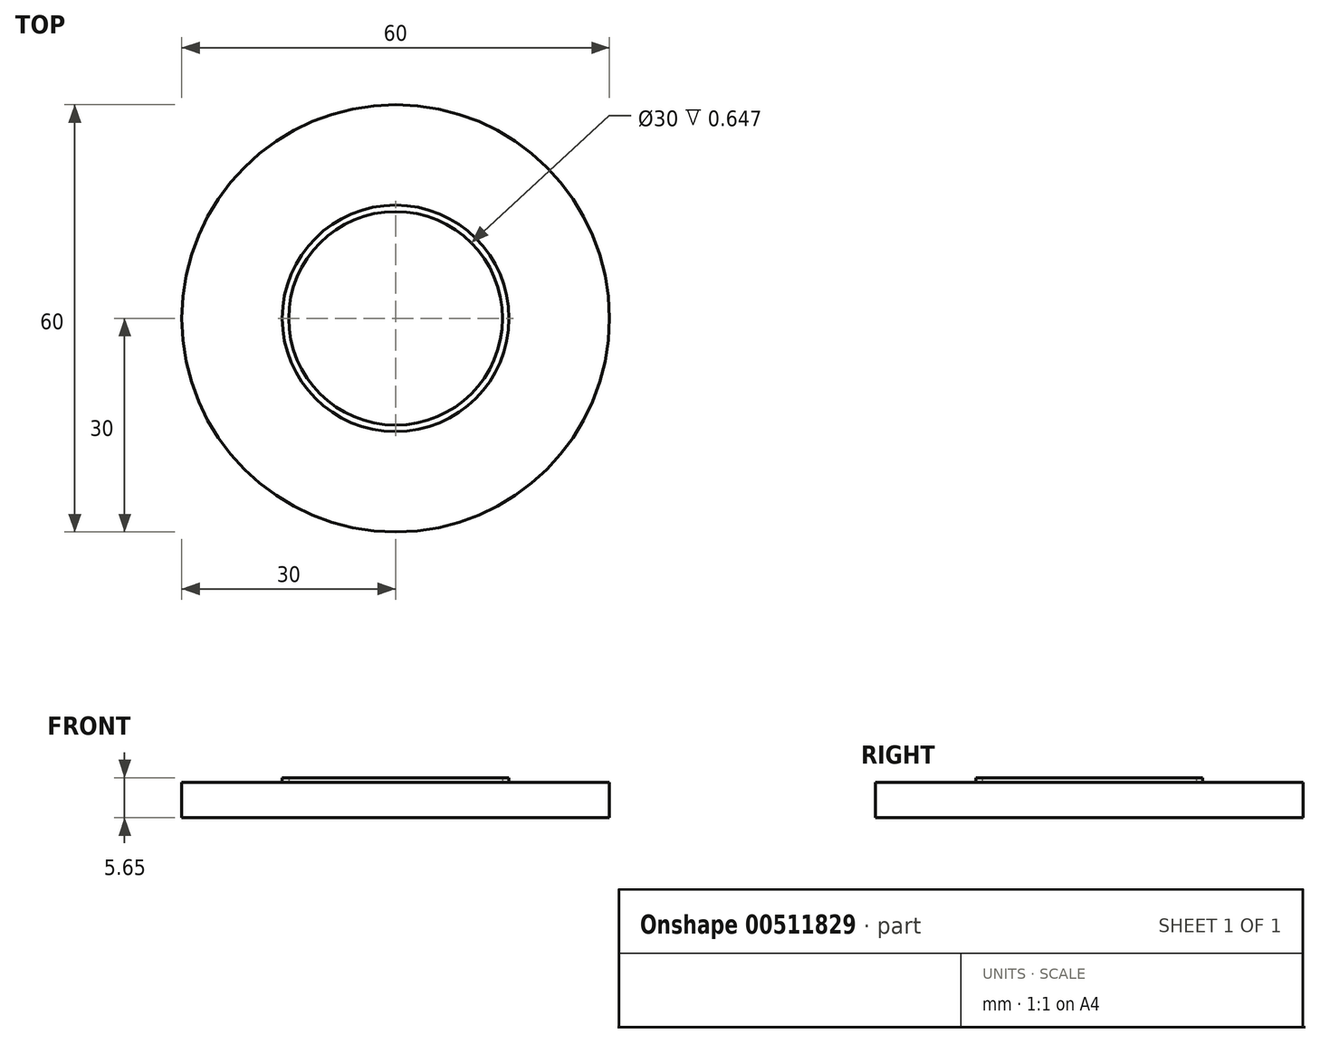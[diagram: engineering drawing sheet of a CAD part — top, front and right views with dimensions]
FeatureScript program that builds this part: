
annotation { "Feature Type Name" : "Feature", "Feature Type Description" : "" }
export const myFeature = defineFeature(function(context is Context, id is Id, definition is map)
    precondition{}
    {
        {
            var Q0;
            Q0=qCreatedBy(makeId("Front.planeOp"),FACE);
            var sketch = newSketch(context, id + "F0", { "sketchPlane" : qUnion([Q0])});
            skLineSegment(sketch, "E0", {"start": v(0, 0) * mm, "end": v(0, 26.23) * mm, "construction": true});
            skPoint(sketch, "E1.end.orphan", {"position": v(106.03, -6.74) * mm});
            skPoint(sketch, "E2.end.orphan", {"position": v(0, -6.74) * mm});
            skLineSegment(sketch, "E3.bottom", {"start": v(0, 0) * mm, "end": v(30, 0) * mm});
            skLineSegment(sketch, "E3.top", {"start": v(0, -5) * mm, "end": v(30, -5) * mm});
            skLineSegment(sketch, "E3.left", {"start": v(0, 0) * mm, "end": v(0, -5) * mm});
            skLineSegment(sketch, "E3.right", {"start": v(30, 0) * mm, "end": v(30, -5) * mm});
            skSolve(sketch);
        }
        {
            var Q0;
            Q0 = qSketchRegion(id + "F0", true);
            var Q1;
            Q1=sQuery(id+"F0.wireOp",EDGE,"E0");
            revolve(context, id + "F1", {"entities" : qUnion([Q0]), "axis" : qUnion([Q1]), "revolveType" : RevolveType.FULL});
        }
        {
            var Q0;
            Q0=qCreatedBy(makeId("Front.planeOp"),FACE);
            var sketch = newSketch(context, id + "F2", { "sketchPlane" : qUnion([Q0])});
            skLineSegment(sketch, "E4", {"start": v(15, 0) * mm, "end": v(15.9, 0) * mm});
            skLineSegment(sketch, "E5.top", {"start": v(15, 0.65) * mm, "end": v(15.9, 0.65) * mm});
            skLineSegment(sketch, "E5.left", {"start": v(15, 0) * mm, "end": v(15, 0.65) * mm});
            skLineSegment(sketch, "E5.right", {"start": v(15.9, 0) * mm, "end": v(15.9, 0.65) * mm});
            skLineSegment(sketch, "E6", {"start": v(0, 0) * mm, "end": v(0, 2.45) * mm, "construction": true});
            skSolve(sketch);
        }
        {
            var Q0;
            Q0 = qSketchRegion(id + "F2", true);
            var Q1;
            Q1=sQuery(id+"F2.wireOp",EDGE,"E6");
            revolve(context, id + "F3", {"operationType" : NewBodyOperationType.ADD, "entities" : qUnion([Q0]), "axis" : qUnion([Q1]), "revolveType" : RevolveType.FULL});
        }
    });
